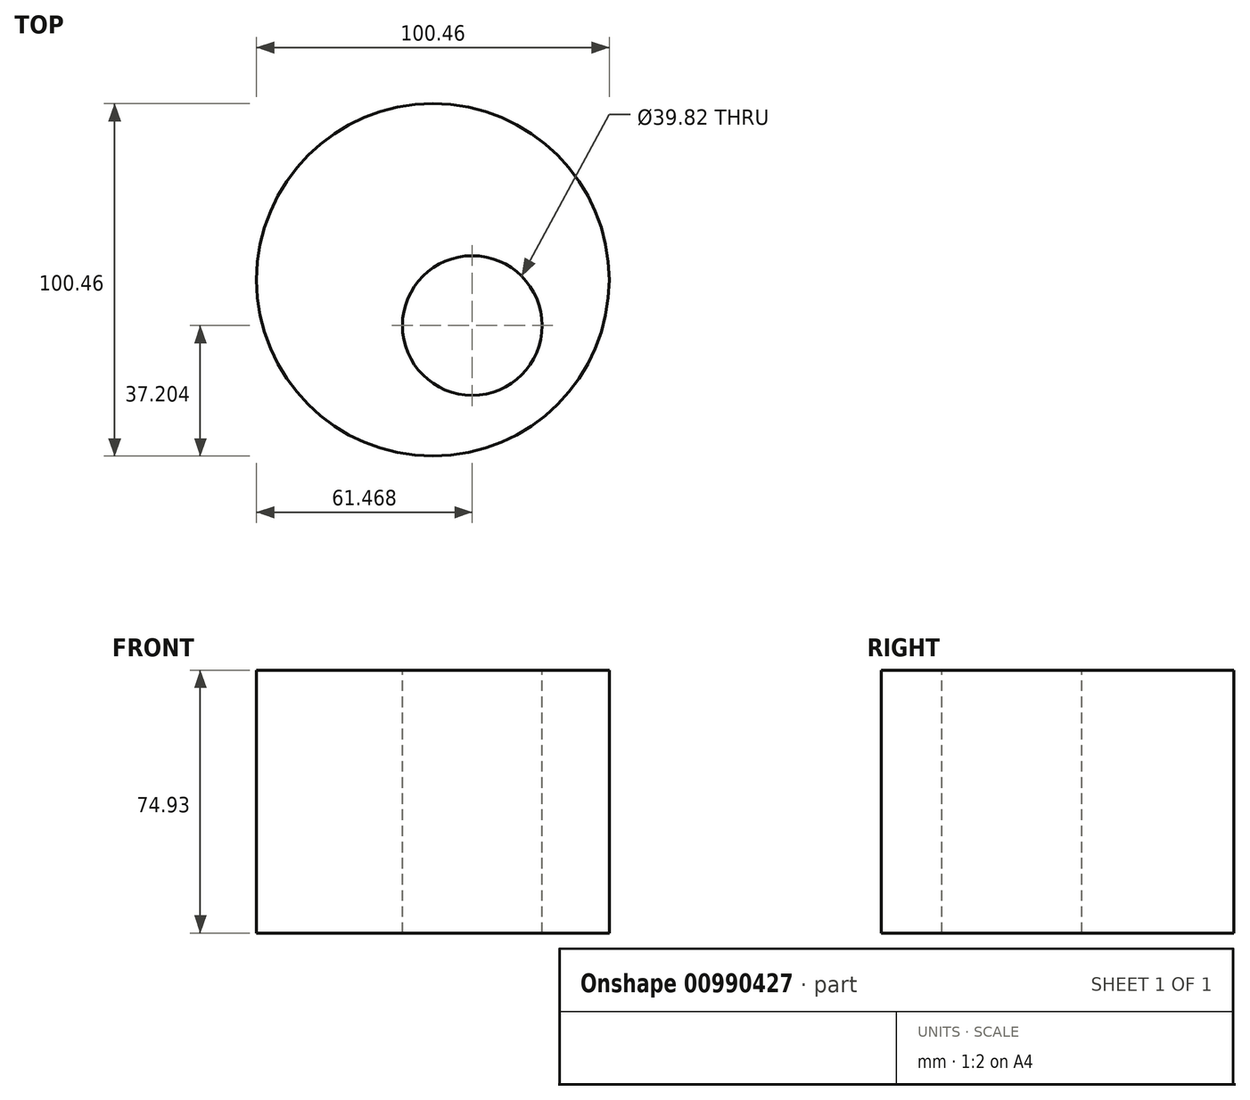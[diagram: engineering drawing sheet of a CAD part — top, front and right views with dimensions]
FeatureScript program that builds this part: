
annotation { "Feature Type Name" : "Feature", "Feature Type Description" : "" }
export const myFeature = defineFeature(function(context is Context, id is Id, definition is map)
    precondition{}
    {
        {
            var Q0;
            Q0=qCreatedBy(makeId("Top.planeOp"),FACE);
            var sketch = newSketch(context, id + "F0", { "sketchPlane" : qUnion([Q0])});
            skCircle(sketch, "E0", {"center": v(0, 0) * mm, "radius": 50.23 * mm});
            skSolve(sketch);
        }
        {
            var Q0;
            Q0 = qSketchRegion(id + "F0", true);
            extrude(context, id + "F1", {"entities" : qUnion([Q0]), "depth" : 100.33 * mm, "offsetDistance" : 25.4 * mm});
        }
        {
            var Q0;
            Q0=makeQuery(id+"F1.opExtrude","CAP_FACE",FACE,{"disambiguationData":[OSD([sQuery(id+"F0.wireOp",EDGE,"E0")])],"isStart":false});
            extrude(context, id + "F2", {"entities" : qUnion([Q0]), "operationType" : NewBodyOperationType.REMOVE, "oppositeDirection" : true, "depth" : 25.4 * mm, "offsetDistance" : 25.4 * mm});
        }
        {
            var Q0;
            Q0=makeQuery(id+"F2.boolean.opBoolean","COPY",FACE,{"derivedFrom":makeQuery(id+"F2.opExtrude","CAP_FACE",FACE,{"disambiguationData":[OSD([sQuery(id+"F0.wireOp",EDGE,"E0")])],"isStart":false})});
            var sketch = newSketch(context, id + "F3", { "sketchPlane" : qUnion([Q0])});
            skCircle(sketch, "E1", {"center": v(11.24, -13.03) * mm, "radius": 19.91 * mm});
            skSolve(sketch);
        }
        {
            var Q0;
            Q0=makeQuery(id+"F3.imprint","IMPRINT",FACE,{"disambiguationData":[TD([[makeQuery(id+"F3.imprint","IMPRINT",EDGE,{"derivedFrom":sQuery(id+"F3.wireOp",EDGE,"E1")}),1.0]])]});
            extrude(context, id + "F4", {"entities" : qUnion([Q0]), "operationType" : NewBodyOperationType.REMOVE, "oppositeDirection" : true, "depth" : 258.83 * mm, "offsetDistance" : 25.4 * mm});
        }
    });
